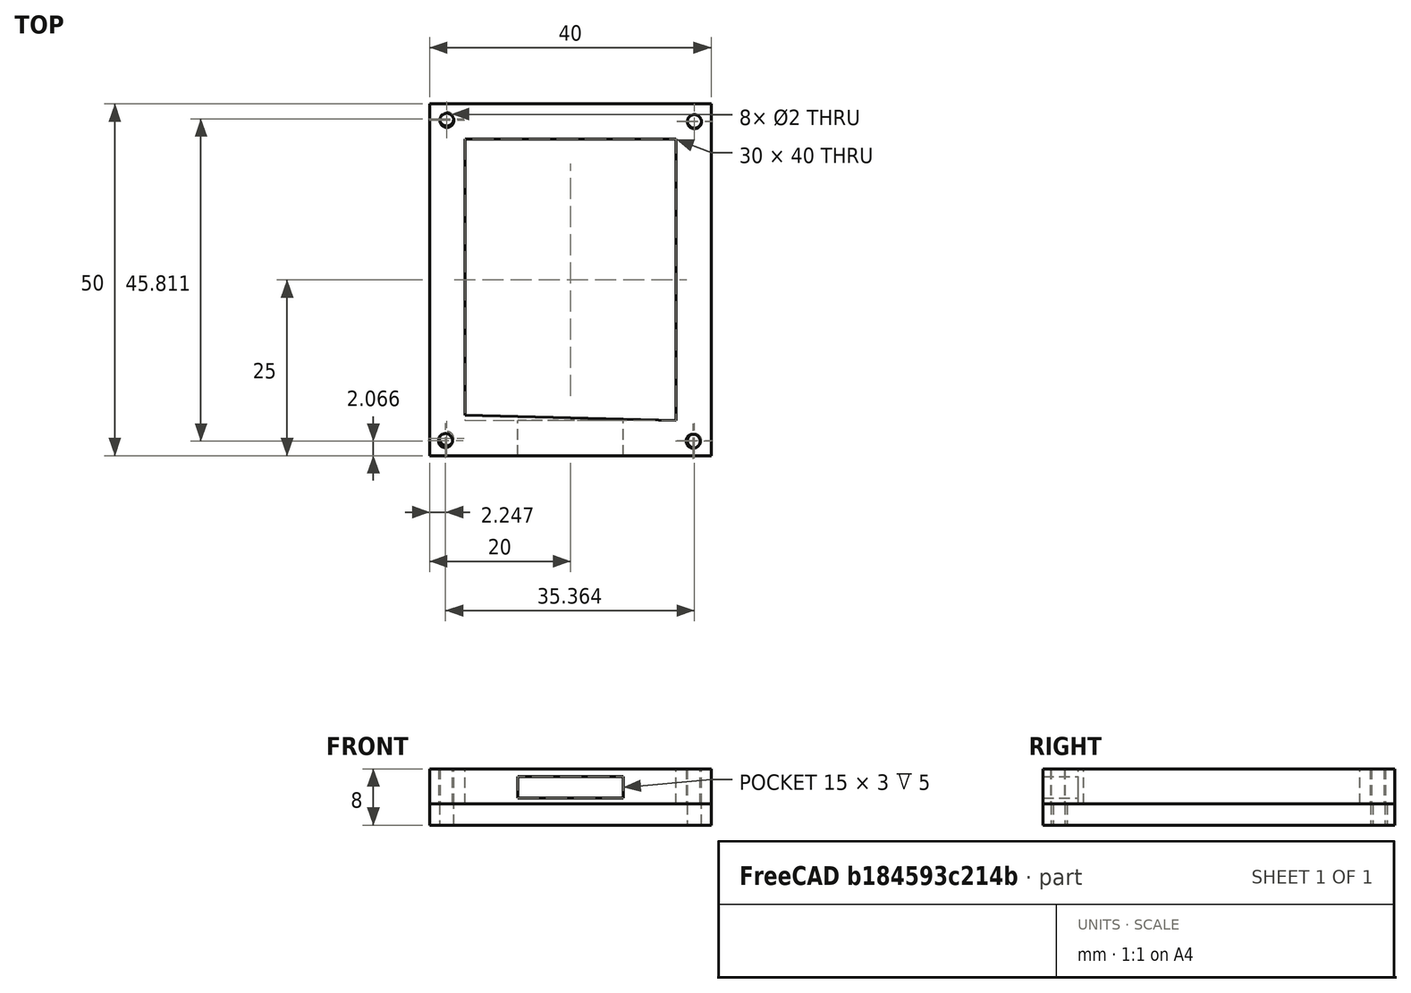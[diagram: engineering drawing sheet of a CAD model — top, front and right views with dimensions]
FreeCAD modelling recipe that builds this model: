
FCSTD DOCUMENT  (FreeCAD 0.19R24291 (Git))
Label: numpad
License: All rights reserved
LicenseURL: http://en.wikipedia.org/wiki/All_rights_reserved
objects: Sketcher::SketchObject×8, PartDesign::Pad×2, PartDesign::Pocket×2, PartDesign::Body×2, PartDesign::Draft×1
note: 20 computed .brp shape members not serialized (recipe doc carries the construction recipe); baked Part::Feature solids carry a one-line shape summary decoded from their .brp

FEATURE [Sketcher::SketchObject] Sketch
  FullyConstrained = true
  MapMode = 5
  Support = -> [XY_Plane]
  sketch-geometry (4):
    g0: LineSegment StartX=-20 StartY=25 StartZ=0 EndX=20 EndY=25 EndZ=0
    g1: LineSegment StartX=20 StartY=25 StartZ=0 EndX=20 EndY=-25 EndZ=0
    g2: LineSegment StartX=20 StartY=-25 StartZ=0 EndX=-20 EndY=-25 EndZ=0
    g3: LineSegment StartX=-20 StartY=-25 StartZ=0 EndX=-20 EndY=25 EndZ=0
  constraints (10):
    c: Coincident(g0,g1)
    c: Coincident(g1,g2)
    c: Coincident(g2,g3)
    c: Coincident(g3,g0)
    c: Horizontal(g2)
    c: Vertical(g1)
    c: DistanceY(g3,g3) = 50
    c: DistanceX(g0,g0) = 40
    c: Symmetric(g0,g0,g-2)
    c: Symmetric(g0,g2,g-1)
FEATURE [PartDesign::Pad] Pad
  Direction = (1,1,1)
  Length = 3
  Length2 = 100
  Profile = -> Sketch
  Type = 0
FEATURE [Sketcher::SketchObject] Sketch002
  AttachmentOffset = pos=(0,0,8) rot=(0,0,1;0rad)
  FullyConstrained = false
  MapMode = 5
  Placement = pos=(0,0,8) rot=(0,0,1;0rad)
  Support = -> [XY_Plane002]
  sketch-geometry (12):
    g0: LineSegment StartX=-20 StartY=25 StartZ=0 EndX=20 EndY=25 EndZ=0
    g1: LineSegment StartX=20 StartY=25 StartZ=0 EndX=20 EndY=-25 EndZ=0
    g2: LineSegment StartX=20 StartY=-25 StartZ=0 EndX=-20 EndY=-25 EndZ=0
    g3: LineSegment StartX=-20 StartY=-25 StartZ=0 EndX=-20 EndY=25 EndZ=0
    g4: LineSegment StartX=-15 StartY=20 StartZ=0 EndX=15 EndY=20 EndZ=0
    g5: LineSegment StartX=15 StartY=20 StartZ=0 EndX=15 EndY=-20 EndZ=0
    g6: LineSegment StartX=15 StartY=-20 StartZ=0 EndX=-15 EndY=-20 EndZ=0
    g7: LineSegment StartX=-15 StartY=-20 StartZ=0 EndX=-15 EndY=20 EndZ=0
    g8: Circle CenterX=-17.5561 CenterY=22.6674 CenterZ=0 NormalX=0 NormalY=0 NormalZ=1 AngleXU=0 Radius=0.915621
    g9: Circle CenterX=17.8356 CenterY=22.5244 CenterZ=0 NormalX=0 NormalY=0 NormalZ=1 AngleXU=0 Radius=1
    g10: Circle CenterX=17.2636 CenterY=-22.4481 CenterZ=0 NormalX=0 NormalY=0 NormalZ=1 AngleXU=0 Radius=2.66872
    g11: Circle CenterX=-17.9136 CenterY=-23.0916 CenterZ=0 NormalX=0 NormalY=0 NormalZ=1 AngleXU=0 Radius=0.915621
  constraints (21):
    c: Coincident(g0,g1)
    c: Coincident(g1,g2)
    c: Coincident(g2,g3)
    c: Coincident(g3,g0)
    c: Horizontal(g2)
    c: Vertical(g1)
    c: DistanceY(g3,g3) = 50
    c: DistanceX(g0,g0) = 40
    c: Symmetric(g0,g0,g-2)
    c: Symmetric(g0,g2,g-1)
    c: Coincident(g4,g5)
    c: Coincident(g5,g6)
    c: Coincident(g6,g7)
    c: Coincident(g7,g4)
    c: Horizontal(g6)
    c: Vertical(g5)
    c: DistanceX(g4,g4) = 30
    c: DistanceY(g7,g7) = 40
    c: Symmetric(g4,g4,g-2)
    c: Symmetric(g4,g6,g-1)
    c: Radius(g9) = 1
FEATURE [PartDesign::Pad] Pad002
  Direction = (1,1,1)
  Length = 5
  Length2 = 100
  Profile = -> Sketch002
  Type = 0
FEATURE [PartDesign::Draft] Draft
  Angle = 1.5
  Base = -> Pad002 [Face6]
  BaseFeature = -> Pad002
  SupportTransform = false
FEATURE [Sketcher::SketchObject] Sketch003
  FullyConstrained = false
  MapMode = 5
  Placement = pos=(0,-25,0) rot=(1,0,0;1.5708rad)
  Support = -> [Pad002]
  sketch-geometry (4):
    g0: LineSegment StartX=-7.50246 StartY=11.8765 StartZ=0 EndX=7.49754 EndY=11.8765 EndZ=0
    g1: LineSegment StartX=7.49754 StartY=11.8765 StartZ=0 EndX=7.49754 EndY=8.87653 EndZ=0
    g2: LineSegment StartX=7.49754 StartY=8.87653 StartZ=0 EndX=-7.50246 EndY=8.87653 EndZ=0
    g3: LineSegment StartX=-7.50246 StartY=8.87653 StartZ=0 EndX=-7.50246 EndY=11.8765 EndZ=0
  constraints (10):
    c: Coincident(g0,g1)
    c: Coincident(g1,g2)
    c: Coincident(g2,g3)
    c: Coincident(g3,g0)
    c: Horizontal(g0)
    c: Horizontal(g2)
    c: Vertical(g1)
    c: Vertical(g3)
    c: DistanceY(g3,g3) = 3
    c: DistanceX(g0,g0) = 15
FEATURE [PartDesign::Pocket] Pocket
  BaseFeature = -> Draft
  Length = 10
  Length2 = 100
  Profile = -> Sketch003
  Type = 0
FEATURE [Sketcher::SketchObject] Sketch004
  FullyConstrained = true
  MapMode = 5
  Placement = pos=(0,0,13) rot=(0,0,1;0rad)
  Support = -> [Pocket]
FEATURE [Sketcher::SketchObject] Sketch005
  FullyConstrained = true
  MapMode = 5
  Placement = pos=(0,0,13) rot=(0,0,1;0rad)
  Support = -> [Pocket]
FEATURE [Sketcher::SketchObject] Sketch006
  FullyConstrained = true
  MapMode = 5
  Placement = pos=(0,0,13) rot=(0,0,1;0rad)
  Support = -> [Pocket]
FEATURE [Sketcher::SketchObject] Sketch007
  FullyConstrained = true
  MapMode = 5
  Support = -> [XY_Plane002]
FEATURE [PartDesign::Body] Body002
  Group = -> [Sketch002,Pad002,Draft,Sketch003,Pocket,Sketch004,Sketch005,Sketch006,Sketch007]
  Origin = -> Origin002
  Placement = pos=(0,0,-5) rot=(0,0,1;0rad)
  Tip = -> Pocket
FEATURE [Sketcher::SketchObject] Sketch008
  FullyConstrained = false
  MapMode = 5
  Placement = pos=(0,0,0) rot=(1,0,0;3.14159rad)
  Support = -> [Pad]
  sketch-geometry (4):
    g0: Circle CenterX=-17.5886 CenterY=22.5621 CenterZ=0 NormalX=0 NormalY=0 NormalZ=1 AngleXU=0 Radius=1
    g1: Circle CenterX=-17.5886 CenterY=-22.8764 CenterZ=0 NormalX=0 NormalY=0 NormalZ=1 AngleXU=0 Radius=1
    g2: Circle CenterX=17.6102 CenterY=-22.5564 CenterZ=0 NormalX=0 NormalY=0 NormalZ=1 AngleXU=0 Radius=1
    g3: Circle CenterX=17.6102 CenterY=22.8821 CenterZ=0 NormalX=0 NormalY=0 NormalZ=1 AngleXU=0 Radius=1
  constraints (4):
    c: Radius(g0) = 1
    c: Radius(g3) = 1
    c: Radius(g1) = 1
    c: Radius(g2) = 1
FEATURE [PartDesign::Pocket] Pocket001
  BaseFeature = -> Pad
  Length = 5
  Length2 = 100
  Profile = -> Sketch008
  Type = 0
FEATURE [PartDesign::Body] Body
  Group = -> [Sketch,Pad,Sketch008,Pocket001]
  Origin = -> Origin
  Tip = -> Pocket001
